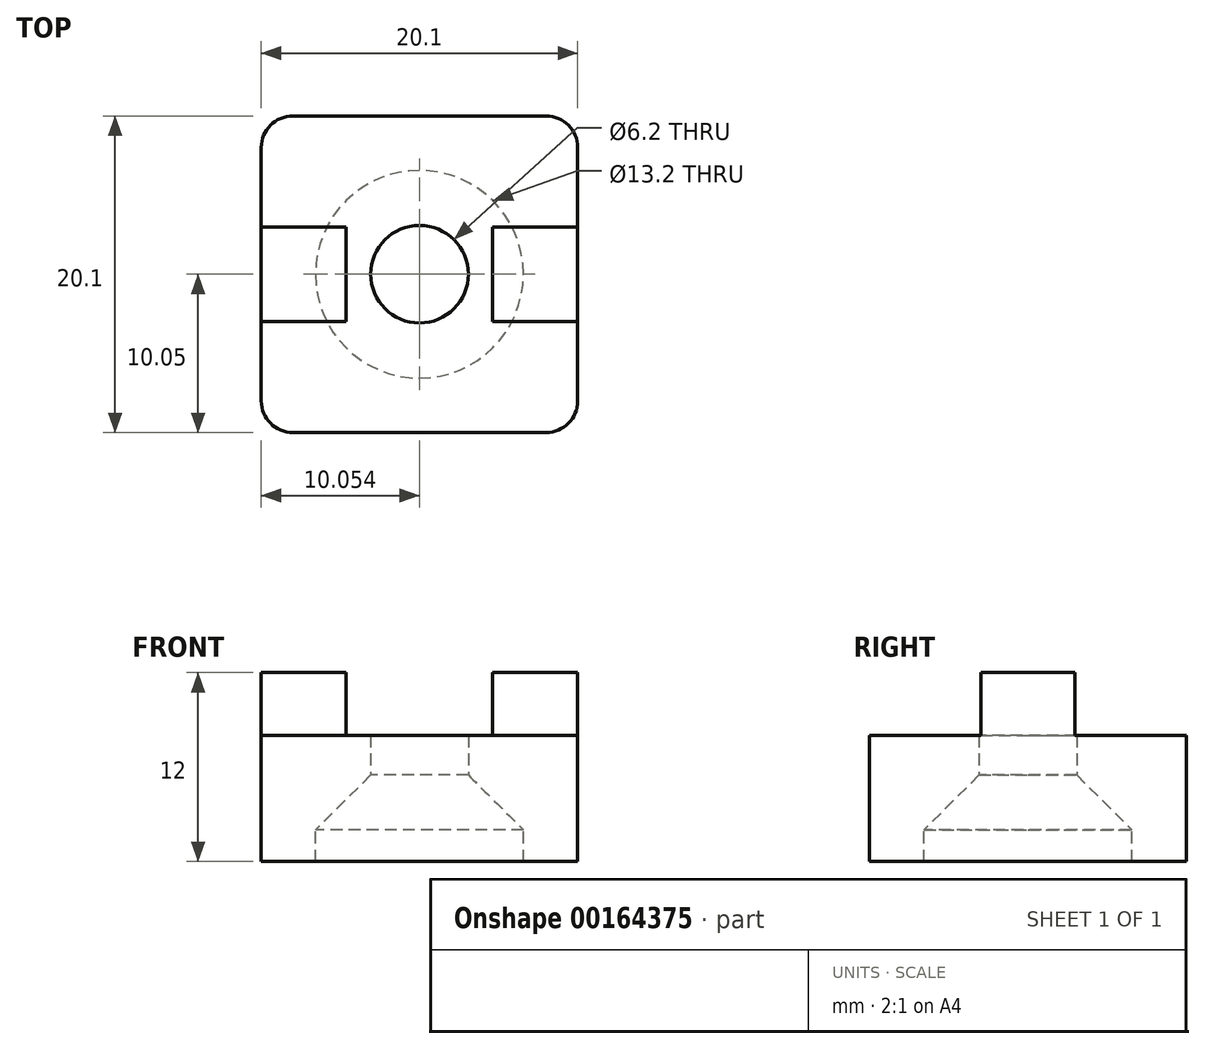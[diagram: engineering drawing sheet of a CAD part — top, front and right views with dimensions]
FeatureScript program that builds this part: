
annotation { "Feature Type Name" : "Feature", "Feature Type Description" : "" }
export const myFeature = defineFeature(function(context is Context, id is Id, definition is map)
    precondition{}
    {
        {
            var Q0;
            Q0=qCreatedBy(makeId("Top.planeOp"),FACE);
            var sketch = newSketch(context, id + "F0", { "sketchPlane" : qUnion([Q0])});
            skLineSegment(sketch, "E0.bottom", {"start": v(-8, 0) * mm, "end": v(12.1, 0) * mm});
            skLineSegment(sketch, "E0.top", {"start": v(-8, 20.1) * mm, "end": v(12.1, 20.1) * mm});
            skLineSegment(sketch, "E0.left", {"start": v(-8, 0) * mm, "end": v(-8, 20.1) * mm});
            skLineSegment(sketch, "E0.right", {"start": v(12.1, 0) * mm, "end": v(12.1, 20.1) * mm});
            skPoint(sketch, "E1", {"position": v(2.05, 20.1) * mm});
            skPoint(sketch, "E2", {"position": v(12.1, 10.05) * mm});
            skLineSegment(sketch, "E3.bottom", {"start": v(-0.95, 20.1) * mm, "end": v(5.05, 20.1) * mm});
            skLineSegment(sketch, "E3.top", {"start": v(-0.95, 14.7) * mm, "end": v(5.05, 14.7) * mm});
            skLineSegment(sketch, "E3.left", {"start": v(-0.95, 20.1) * mm, "end": v(-0.95, 14.7) * mm});
            skLineSegment(sketch, "E3.right", {"start": v(5.05, 20.1) * mm, "end": v(5.05, 14.7) * mm});
            skLineSegment(sketch, "E4.bottom", {"start": v(-0.95, 0) * mm, "end": v(5.05, 0) * mm});
            skLineSegment(sketch, "E4.top", {"start": v(-0.95, 5.4) * mm, "end": v(5.05, 5.4) * mm});
            skLineSegment(sketch, "E4.left", {"start": v(-0.95, 0) * mm, "end": v(-0.95, 5.4) * mm});
            skLineSegment(sketch, "E4.right", {"start": v(5.05, 0) * mm, "end": v(5.05, 5.4) * mm});
            skLineSegment(sketch, "E5.bottom", {"start": v(-8, 13.05) * mm, "end": v(-2.6, 13.05) * mm});
            skLineSegment(sketch, "E5.top", {"start": v(-8, 7.05) * mm, "end": v(-2.6, 7.05) * mm});
            skLineSegment(sketch, "E5.left", {"start": v(-8, 13.05) * mm, "end": v(-8, 7.05) * mm});
            skLineSegment(sketch, "E5.right", {"start": v(-2.6, 13.05) * mm, "end": v(-2.6, 7.05) * mm});
            skLineSegment(sketch, "E6.bottom", {"start": v(12.1, 13.05) * mm, "end": v(6.7, 13.05) * mm});
            skLineSegment(sketch, "E6.top", {"start": v(12.1, 7.05) * mm, "end": v(6.7, 7.05) * mm});
            skLineSegment(sketch, "E6.left", {"start": v(12.1, 13.05) * mm, "end": v(12.1, 7.05) * mm});
            skLineSegment(sketch, "E6.right", {"start": v(6.7, 13.05) * mm, "end": v(6.7, 7.05) * mm});
            skPoint(sketch, "E7", {"position": v(2.05, 14.7) * mm});
            skPoint(sketch, "E8", {"position": v(6.7, 10.05) * mm});
            skCircle(sketch, "E9", {"center": v(2.05, 10.05) * mm, "radius": 3.1 * mm});
            skPoint(sketch, "E9.centerSnap0", {"position": v(-2.6, 10.05) * mm});
            skSolve(sketch);
        }
        {
            var Q0;
            Q0=makeQuery(id+"F0.imprint","IMPRINT",FACE,{"disambiguationData":[TD([[makeQuery(id+"F0.imprint","IMPRINT",EDGE,{"derivedFrom":sQuery(id+"F0.wireOp",EDGE,"E3.top")}),-1.0]])]});
            var Q1;
            {var subQ0=sQuery(id+"F0.wireOp",EDGE,"E4.left");Q1=makeQuery(id+"F0.imprint","IMPRINT",FACE,{"disambiguationData":[TD([[makeQuery(id+"F0.imprint","IMPRINT",EDGE,{"derivedFrom":subQ0}),1.0]])]});}
            var Q2;
            {var subQ0=sQuery(id+"F0.wireOp",EDGE,"E4.right");Q2=makeQuery(id+"F0.imprint","IMPRINT",FACE,{"disambiguationData":[TD([[makeQuery(id+"F0.imprint","IMPRINT",EDGE,{"derivedFrom":subQ0}),-1.0]])]});}
            var Q3;
            {var subQ1=sQuery(id+"F0.wireOp",EDGE,"E6.bottom");Q3=makeQuery(id+"F0.imprint","IMPRINT",FACE,{"disambiguationData":[TD([[makeQuery(id+"F0.imprint","IMPRINT",EDGE,{"derivedFrom":subQ1}),1.0]])]});}
            var Q4;
            {var subQ1=sQuery(id+"F0.wireOp",EDGE,"E5.bottom");Q4=makeQuery(id+"F0.imprint","IMPRINT",FACE,{"disambiguationData":[TD([[makeQuery(id+"F0.imprint","IMPRINT",EDGE,{"derivedFrom":subQ1}),-1.0]])]});}
            var Q5;
            Q5=makeQuery(id+"F0.imprint","IMPRINT",FACE,{"disambiguationData":[TD([[makeQuery(id+"F0.imprint","IMPRINT",EDGE,{"derivedFrom":sQuery(id+"F0.wireOp",EDGE,"E3.bottom")}),-1.0]])]});
            var Q6;
            Q6=makeQuery(id+"F0.imprint","IMPRINT",FACE,{"disambiguationData":[TD([[makeQuery(id+"F0.imprint","IMPRINT",EDGE,{"derivedFrom":sQuery(id+"F0.wireOp",EDGE,"E4.bottom")}),1.0]])]});
            var Q7;
            {var subQ0=sQuery(id+"F0.wireOp",EDGE,"iCEa6wk3-0xmd-ce5d-x8J3-6bLyloWlNHDb");var subQ1=sQuery(id+"F0.wireOp",EDGE,"E3.top");var subQ2=makeQuery(id+"F0.imprint","INTERSECT",VERTEX,{"disambiguationData":[OD(0.0)],"derivedFrom":[subQ1,subQ0]});Q7=makeQuery(id+"F0.imprint","IMPRINT",FACE,{"disambiguationData":[TD([[makeQuery(id+"F0.imprint","IMPRINT",EDGE,{"disambiguationData":[TD([[subQ2,-1.0]])],"derivedFrom":subQ1}),1.0]])]});}
            var Q8;
            Q8=makeQuery(id+"F0.imprint","IMPRINT",FACE,{"disambiguationData":[TD([[makeQuery(id+"F0.imprint","IMPRINT",EDGE,{"derivedFrom":sQuery(id+"F0.wireOp",EDGE,"E9")}),-1.0]])]});
            var Q9;
            {var subQ0=sQuery(id+"F0.wireOp",EDGE,"iCEa6wk3-0xmd-ce5d-x8J3-6bLyloWlNHDb");var subQ1=sQuery(id+"F0.wireOp",EDGE,"E5.right");var subQ2=makeQuery(id+"F0.imprint","INTERSECT",VERTEX,{"disambiguationData":[OD(0.0)],"derivedFrom":[subQ1,subQ0]});Q9=makeQuery(id+"F0.imprint","IMPRINT",FACE,{"disambiguationData":[TD([[makeQuery(id+"F0.imprint","IMPRINT",EDGE,{"disambiguationData":[TD([[subQ2,-1.0]])],"derivedFrom":subQ1}),-1.0]])]});}
            var Q10;
            {var subQ0=sQuery(id+"F0.wireOp",EDGE,"iCEa6wk3-0xmd-ce5d-x8J3-6bLyloWlNHDb");var subQ1=sQuery(id+"F0.wireOp",EDGE,"E4.top");var subQ2=makeQuery(id+"F0.imprint","INTERSECT",VERTEX,{"disambiguationData":[OD(0.0)],"derivedFrom":[subQ1,subQ0]});Q10=makeQuery(id+"F0.imprint","IMPRINT",FACE,{"disambiguationData":[TD([[makeQuery(id+"F0.imprint","IMPRINT",EDGE,{"disambiguationData":[TD([[subQ2,-1.0]])],"derivedFrom":subQ1}),-1.0]])]});}
            var Q11;
            {var subQ0=sQuery(id+"F0.wireOp",EDGE,"iCEa6wk3-0xmd-ce5d-x8J3-6bLyloWlNHDb");var subQ1=sQuery(id+"F0.wireOp",EDGE,"E6.right");var subQ2=makeQuery(id+"F0.imprint","INTERSECT",VERTEX,{"disambiguationData":[OD(0.0)],"derivedFrom":[subQ1,subQ0]});Q11=makeQuery(id+"F0.imprint","IMPRINT",FACE,{"disambiguationData":[TD([[makeQuery(id+"F0.imprint","IMPRINT",EDGE,{"disambiguationData":[TD([[subQ2,-1.0]])],"derivedFrom":subQ1}),1.0]])]});}
            extrude(context, id + "F1", {"entities" : qUnion([Q0, Q1, Q2, Q3, Q4, Q5, Q6, Q7, Q8, Q9, Q10, Q11]), "depth" : 6 * mm});
        }
        {
            var Q0;
            Q0=makeQuery(id+"F0.imprint","IMPRINT",FACE,{"disambiguationData":[TD([[makeQuery(id+"F0.imprint","IMPRINT",EDGE,{"derivedFrom":sQuery(id+"F0.wireOp",EDGE,"E3.bottom")}),-1.0]])]});
            var Q1;
            Q1=makeQuery(id+"F0.imprint","IMPRINT",FACE,{"disambiguationData":[TD([[makeQuery(id+"F0.imprint","IMPRINT",EDGE,{"derivedFrom":sQuery(id+"F0.wireOp",EDGE,"E5.bottom")}),-1.0]])]});
            var Q2;
            Q2=makeQuery(id+"F0.imprint","IMPRINT",FACE,{"disambiguationData":[TD([[makeQuery(id+"F0.imprint","IMPRINT",EDGE,{"derivedFrom":sQuery(id+"F0.wireOp",EDGE,"E4.bottom")}),1.0]])]});
            var Q3;
            Q3=makeQuery(id+"F0.imprint","IMPRINT",FACE,{"disambiguationData":[TD([[makeQuery(id+"F0.imprint","IMPRINT",EDGE,{"derivedFrom":sQuery(id+"F0.wireOp",EDGE,"E6.bottom")}),1.0]])]});
            extrude(context, id + "F2", {"entities" : qUnion([Q0, Q1, Q2, Q3]), "operationType" : NewBodyOperationType.ADD, "depth" : 10 * mm});
        }
        {
            var Q0;
            Q0=makeQuery(id+"F1.opExtrude","SWEPT_EDGE",EDGE,{"disambiguationData":[OSD([sQuery(id+"F0.wireOp",EDGE,"E0.bottom"),sQuery(id+"F0.wireOp",EDGE,"E0.left")])]});
            var Q1;
            Q1=makeQuery(id+"F1.opExtrude","SWEPT_EDGE",EDGE,{"disambiguationData":[OSD([sQuery(id+"F0.wireOp",EDGE,"E0.bottom"),sQuery(id+"F0.wireOp",EDGE,"E0.right")])]});
            var Q2;
            Q2=makeQuery(id+"F1.opExtrude","SWEPT_EDGE",EDGE,{"disambiguationData":[OSD([sQuery(id+"F0.wireOp",EDGE,"E0.top"),sQuery(id+"F0.wireOp",EDGE,"E0.right")])]});
            var Q3;
            Q3=makeQuery(id+"F1.opExtrude","SWEPT_EDGE",EDGE,{"disambiguationData":[OSD([sQuery(id+"F0.wireOp",EDGE,"E0.top"),sQuery(id+"F0.wireOp",EDGE,"E0.left")])]});
            fillet(context, id + "F3", {"entities" : qUnion([Q0, Q1, Q2, Q3]), "radius" : 2 * mm, "tangentPropagation" : true, "allowEdgeOverflow" : false});
        }
        {
            var Q0;
            Q0=makeQuery(id+"F1.opExtrude","CAP_EDGE",EDGE,{"disambiguationData":[OSD([sQuery(id+"F0.wireOp",EDGE,"E9")])],"isStart":true});
            chamfer(context, id + "F4", {"entities" : qUnion([Q0]), "width" : 3.5 * mm, "tangentPropagation" : true});
        }
        {
            var Q0;
            Q0=makeQuery(id+"F1.opExtrude","CAP_FACE",FACE,{"disambiguationData":[OSD([sQuery(id+"F0.wireOp",EDGE,"E0.bottom"),sQuery(id+"F0.wireOp",EDGE,"E0.top"),sQuery(id+"F0.wireOp",EDGE,"E0.left"),sQuery(id+"F0.wireOp",EDGE,"E0.right"),sQuery(id+"F0.wireOp",EDGE,"E3.bottom"),sQuery(id+"F0.wireOp",EDGE,"E4.bottom"),sQuery(id+"F0.wireOp",EDGE,"E5.left"),sQuery(id+"F0.wireOp",EDGE,"E6.left"),sQuery(id+"F0.wireOp",EDGE,"E9")])],"isStart":true});
            extrude(context, id + "F5", {"entities" : qUnion([Q0]), "operationType" : NewBodyOperationType.ADD, "depth" : 2 * mm});
        }
    });
